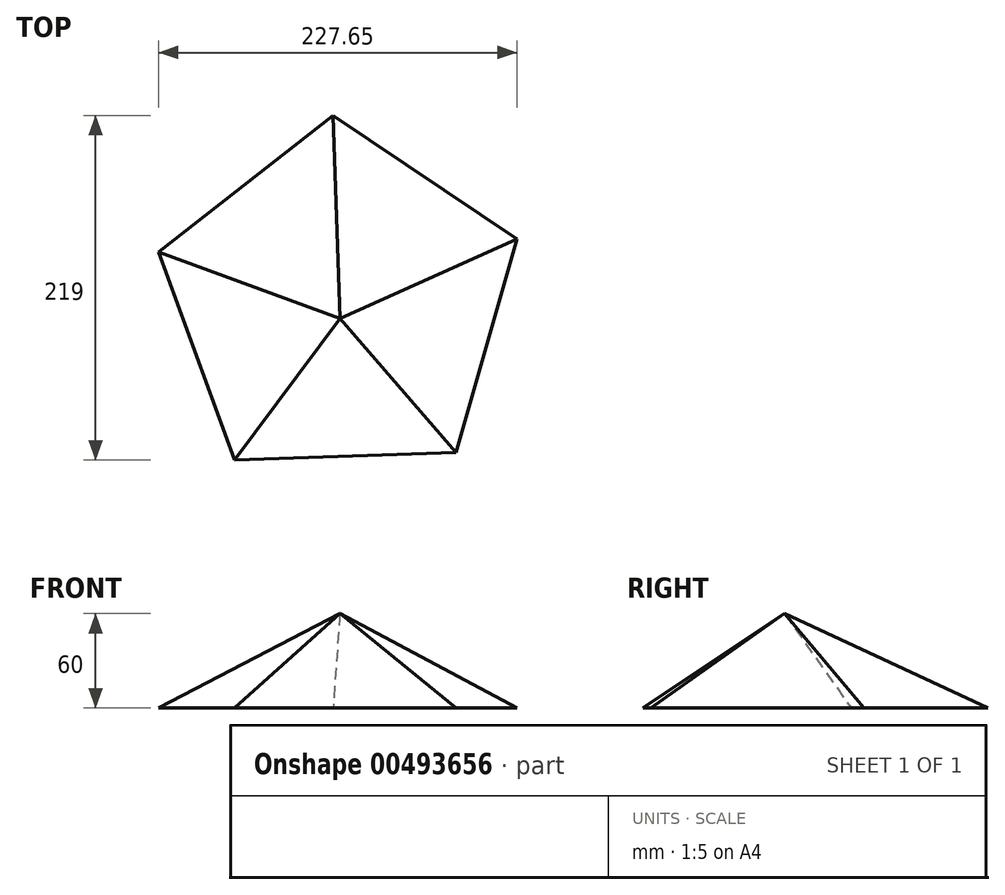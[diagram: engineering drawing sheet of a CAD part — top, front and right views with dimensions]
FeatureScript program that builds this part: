
annotation { "Feature Type Name" : "Feature", "Feature Type Description" : "" }
export const myFeature = defineFeature(function(context is Context, id is Id, definition is map)
    precondition{}
    {
        {
            var Q0;
            Q0=qCreatedBy(makeId("Top.planeOp"),FACE);
            var sketch = newSketch(context, id + "F0", { "sketchPlane" : qUnion([Q0])});
            skCircle(sketch, "E0.cCircle", {"center": v(0, 0) * mm, "radius": 119.76 * mm, "construction": true});
            skLineSegment(sketch, "E0.0", {"start": v(112.51, 41.02) * mm, "end": v(73.78, -94.33) * mm});
            skLineSegment(sketch, "E0.1", {"start": v(73.78, -94.33) * mm, "end": v(-66.91, -99.32) * mm});
            skLineSegment(sketch, "E0.2", {"start": v(-66.91, -99.32) * mm, "end": v(-115.14, 32.94) * mm});
            skLineSegment(sketch, "E0.3", {"start": v(-115.14, 32.94) * mm, "end": v(-4.25, 119.68) * mm});
            skLineSegment(sketch, "E0.4", {"start": v(-4.25, 119.68) * mm, "end": v(112.51, 41.02) * mm});
            skSolve(sketch);
        }
        {
            var Q0;
            Q0=qCreatedBy(makeId("Top.planeOp"),FACE);
            cPlane(context, id + "F1", {"entities" : qUnion([Q0]), "cplaneType" : CPlaneType.OFFSET, "offset" : 60 * mm, "width" : 150 * mm, "height" : 150 * mm});
        }
        {
            var Q0;
            Q0=qCreatedBy(id+"F1.planeOp",FACE);
            var sketch = newSketch(context, id + "F2", { "sketchPlane" : qUnion([Q0])});
            skPoint(sketch, "E1", {"position": v(0, -9.44) * mm});
            skSolve(sketch);
        }
        {
            var Q0;
            Q0=sQuery(id+"F2.wireOp",VERTEX,"E1");
            var Q1;
            Q1=makeQuery(id+"F0.imprint","IMPRINT",FACE,{"disambiguationData":[TD([[makeQuery(id+"F0.imprint","IMPRINT",EDGE,{"derivedFrom":sQuery(id+"F0.wireOp",EDGE,"E0.0")}),-1.0]])]});
            loft(context, id + "F3", {"sheetProfilesArray" : [{ "sheetProfileEntities" : qUnion([Q0]) }, { "sheetProfileEntities" : qUnion([Q1]) }]});
        }
    });
